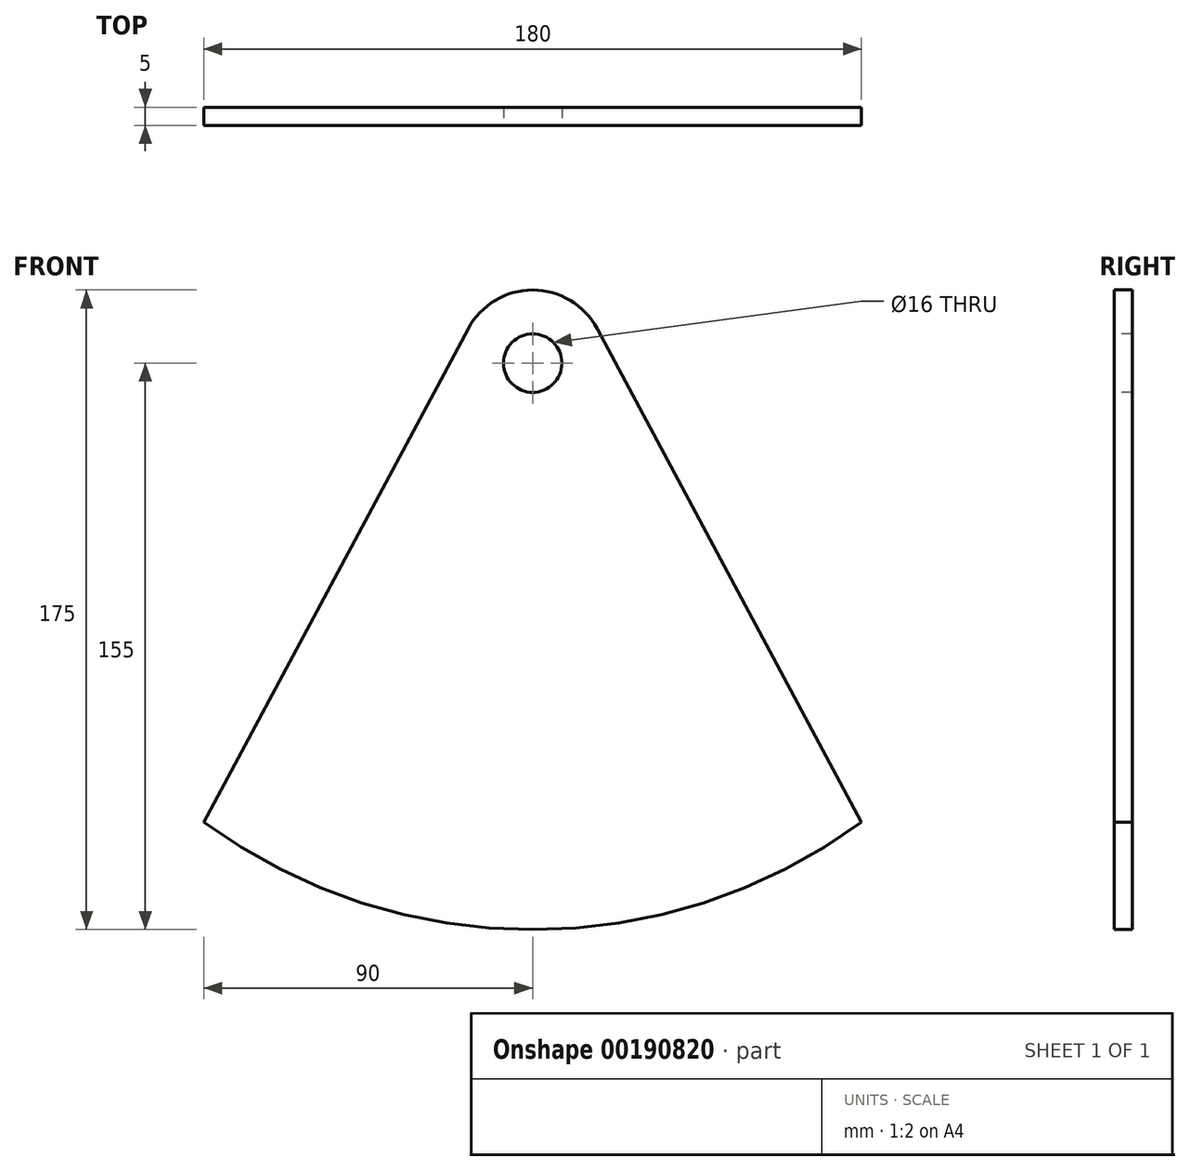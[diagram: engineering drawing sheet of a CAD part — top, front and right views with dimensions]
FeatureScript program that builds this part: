
annotation { "Feature Type Name" : "Feature", "Feature Type Description" : "" }
export const myFeature = defineFeature(function(context is Context, id is Id, definition is map)
    precondition{}
    {
        {
            var Q0;
            Q0=qCreatedBy(makeId("Front.planeOp"),FACE);
            var sketch = newSketch(context, id + "F0", { "sketchPlane" : qUnion([Q0])});
            skArc(sketch, "E0", {"start": v(17.63, 11.95) * mm, "mid": v(0, 22.5) * mm, "end": v(-17.63, 11.95) * mm});
            skArc(sketch, "E1", {"start": v(-90, -123.11) * mm, "mid": v(0, -152.5) * mm, "end": v(90, -123.11) * mm});
            skLineSegment(sketch, "E2", {"start": v(17.63, 11.95) * mm, "end": v(90, -123.11) * mm});
            skLineSegment(sketch, "E3", {"start": v(-17.63, 11.95) * mm, "end": v(-90, -123.11) * mm});
            skSolve(sketch);
        }
        {
            var Q0;
            Q0 = qSketchRegion(id + "F0", true);
            extrude(context, id + "F1", {"entities" : qUnion([Q0]), "depth" : 5 * mm});
        }
        {
            var Q0;
            Q0=makeQuery(id+"F1.opExtrude","CAP_FACE",FACE,{"disambiguationData":[OSD([sQuery(id+"F0.wireOp",EDGE,"E0"),sQuery(id+"F0.wireOp",EDGE,"E1"),sQuery(id+"F0.wireOp",EDGE,"E2"),sQuery(id+"F0.wireOp",EDGE,"E3")])],"isStart":false});
            var sketch = newSketch(context, id + "F2", { "sketchPlane" : qUnion([Q0])});
            skCircle(sketch, "E4", {"center": v(0, 2.5) * mm, "radius": 8 * mm});
            skSolve(sketch);
        }
        {
            var Q0;
            Q0 = qSketchRegion(id + "F2", true);
            extrude(context, id + "F3", {"entities" : qUnion([Q0]), "operationType" : NewBodyOperationType.REMOVE, "endBound" : BoundingType.THROUGH_ALL, "oppositeDirection" : true, "depth" : 25 * mm});
        }
    });
